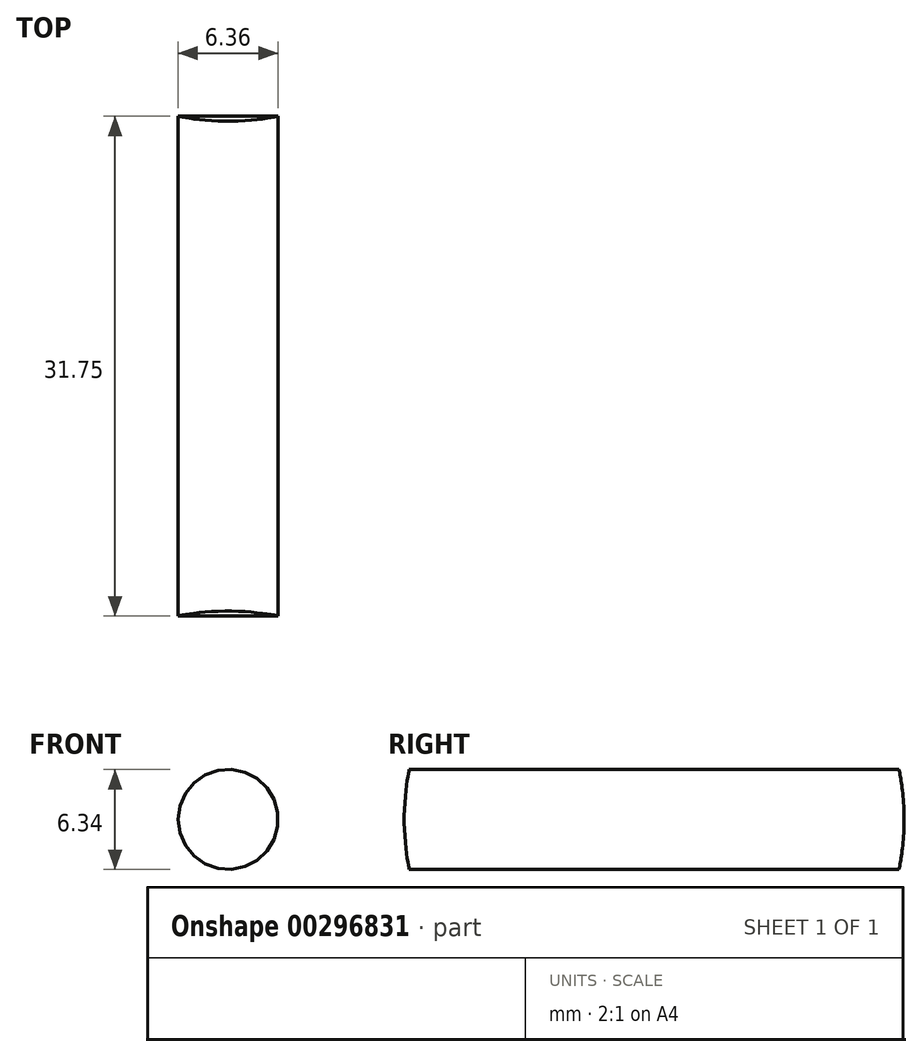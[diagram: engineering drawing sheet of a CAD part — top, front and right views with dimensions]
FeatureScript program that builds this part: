
annotation { "Feature Type Name" : "Feature", "Feature Type Description" : "" }
export const myFeature = defineFeature(function(context is Context, id is Id, definition is map)
    precondition{}
    {
        {
            var Q0;
            Q0=qCreatedBy(makeId("Front.planeOp"),FACE);
            var sketch = newSketch(context, id + "F0", { "sketchPlane" : qUnion([Q0])});
            skCircle(sketch, "E0", {"center": v(0, 0) * mm, "radius": 3.18 * mm});
            skSolve(sketch);
        }
        {
            var Q0;
            Q0=makeQuery(id+"F0.imprint","IMPRINT",FACE,{"disambiguationData":[TD([[makeQuery(id+"F0.imprint","IMPRINT",EDGE,{"derivedFrom":sQuery(id+"F0.wireOp",EDGE,"E0")}),1.0]])]});
            extrude(context, id + "F1", {"entities" : qUnion([Q0]), "depth" : 31.75 * mm});
        }
        {
            var Q0;
            Q0=qCreatedBy(makeId("Right.planeOp"),FACE);
            var sketch = newSketch(context, id + "F2", { "sketchPlane" : qUnion([Q0])});
            skLineSegment(sketch, "E1", {"start": v(0, 0) * mm, "end": v(-15.88, 0) * mm});
            skCircle(sketch, "E2", {"center": v(-15.88, 0) * mm, "radius": 15.88 * mm});
            skLineSegment(sketch, "E3.bottom", {"start": v(0, 17.32) * mm, "end": v(-31.75, 17.32) * mm});
            skLineSegment(sketch, "E3.top", {"start": v(0, -17.32) * mm, "end": v(-31.75, -17.32) * mm});
            skLineSegment(sketch, "E3.left", {"start": v(0, 17.32) * mm, "end": v(0, -17.32) * mm});
            skLineSegment(sketch, "E3.right", {"start": v(-31.75, 17.32) * mm, "end": v(-31.75, -17.32) * mm});
            skSolve(sketch);
        }
        {
            var Q0;
            {var subQ5=sQuery(id+"F2.wireOp",EDGE,"E3.bottom");Q0=makeQuery(id+"F2.imprint","IMPRINT",FACE,{"disambiguationData":[TD([[makeQuery(id+"F2.imprint","IMPRINT",EDGE,{"derivedFrom":subQ5}),1.0]])]});}
            var Q1;
            {var subQ5=sQuery(id+"F2.wireOp",EDGE,"E3.top");Q1=makeQuery(id+"F2.imprint","IMPRINT",FACE,{"disambiguationData":[TD([[makeQuery(id+"F2.imprint","IMPRINT",EDGE,{"derivedFrom":subQ5}),-1.0]])]});}
            extrude(context, id + "F3", {"entities" : qUnion([Q0, Q1]), "operationType" : NewBodyOperationType.REMOVE, "endBound" : BoundingType.SYMMETRIC, "oppositeDirection" : true, "depth" : 25.4 * mm});
        }
    });
